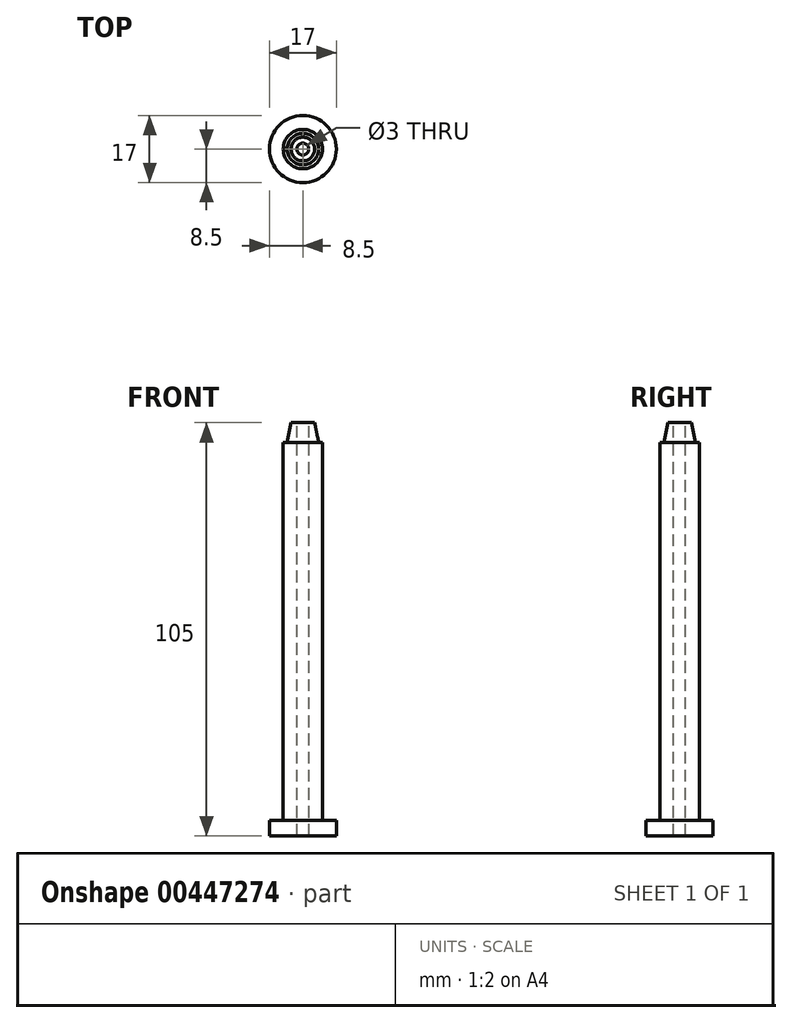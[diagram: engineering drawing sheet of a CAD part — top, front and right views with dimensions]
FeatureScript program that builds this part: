
annotation { "Feature Type Name" : "Feature", "Feature Type Description" : "" }
export const myFeature = defineFeature(function(context is Context, id is Id, definition is map)
    precondition{}
    {
        {
            var Q0;
            Q0=qCreatedBy(makeId("Top.planeOp"),FACE);
            var sketch = newSketch(context, id + "F0", { "sketchPlane" : qUnion([Q0])});
            skCircle(sketch, "E0", {"center": v(0, 0) * mm, "radius": 8.5 * mm});
            skSolve(sketch);
        }
        {
            var Q0;
            Q0=qSketchRegion(id+"F0",true);
            extrude(context, id + "F1", {"entities" : qUnion([Q0]), "depth" : 4 * mm});
        }
        {
            var Q0;
            Q0=qCreatedBy(makeId("Top.planeOp"),FACE);
            var sketch = newSketch(context, id + "F2", { "sketchPlane" : qUnion([Q0])});
            skCircle(sketch, "E1", {"center": v(0, 0) * mm, "radius": 5 * mm});
            skSolve(sketch);
        }
        {
            var Q0;
            Q0=qSketchRegion(id+"F2",true);
            extrude(context, id + "F3", {"entities" : qUnion([Q0]), "operationType" : NewBodyOperationType.ADD, "depth" : 100 * mm});
        }
        {
            var Q0;
            Q0=qCreatedBy(makeId("Right.planeOp"),FACE);
            var sketch = newSketch(context, id + "F4", { "sketchPlane" : qUnion([Q0])});
            skLineSegment(sketch, "E2", {"start": v(0, 105) * mm, "end": v(0, 100) * mm});
            skLineSegment(sketch, "E3", {"start": v(0, 100) * mm, "end": v(4, 100) * mm});
            skLineSegment(sketch, "E4", {"start": v(4, 100) * mm, "end": v(3, 105) * mm});
            skLineSegment(sketch, "E5", {"start": v(3, 105) * mm, "end": v(0, 105) * mm});
            skSolve(sketch);
        }
        {
            var Q0;
            Q0=qSketchRegion(id+"F4",true);
            var Q1;
            Q1=sQuery(id+"F4.wireOp",EDGE,"E2");
            revolve(context, id + "F5", {"operationType" : NewBodyOperationType.ADD, "entities" : qUnion([Q0]), "axis" : qUnion([Q1]), "revolveType" : RevolveType.FULL});
        }
        {
            var Q0;
            Q0=makeQuery(id+"F5.opRevolve","SWEPT_FACE",FACE,{"disambiguationData":[OSD([sQuery(id+"F4.wireOp",EDGE,"E5")])]});
            var sketch = newSketch(context, id + "F6", { "sketchPlane" : qUnion([Q0])});
            skCircle(sketch, "E6", {"center": v(0, 0) * mm, "radius": 1.5 * mm});
            skSolve(sketch);
        }
        {
            var Q0;
            Q0 = qSketchRegion(id + "F6", true);
            extrude(context, id + "F7", {"entities" : qUnion([Q0]), "operationType" : NewBodyOperationType.REMOVE, "oppositeDirection" : true, "depth" : 123 * mm});
        }
    });
